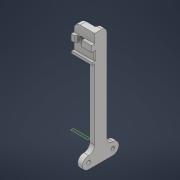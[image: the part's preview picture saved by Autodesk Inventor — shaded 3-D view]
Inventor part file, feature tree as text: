
AUTODESK INVENTOR PART (.ipt)
format: ipt  version: 2021 (Build 250183000, 183)  size: 370,688 bytes
history: native  units: mm
features: sketch x11, extrude x9, move_body x8, fillet x7, projected_geometry x7, direct_edit x5, hole x2, draft x2, chamfer x1, plane x1, split x1, mirror x1
ambient origin geometry x8: Origin, YZ Plane, XZ Plane, XY Plane, X Axis, Y Axis, Z Axis, Center Point
bodies: Solid1 (feature_tree)
feature tree (55):
  extrude  "Extrusion1"  Depth=10.0mm
  hole  "Hole1"  [1 undecoded]
  draft  "FaceDraft1"
  extrude  "Extrusion2"  Depth=10.0mm TaperAngle=0.0deg
  fillet  "Fillet2"  Radius=0.5mm
  extrude  "Extrusion3"  Depth=20.0mm
  extrude  "Extrusion4"  Depth=5.0mm
  extrude  "Extrusion5"  Depth=5.1mm
  extrude  "Extrusion6"  Depth=2.0mm TaperAngle=0.0deg
  fillet  "Fillet4"  Radius=1.0mm
  direct_edit  "Direct Edit1"
  chamfer  "Chamfer1"  Distance=1.0mm
  direct_edit  "Direct Edit2"
  plane  "Work Plane1"
  split  "Split1"
  extrude  "Extrusion7"  Depth=0.5mm TaperAngle=0.0deg
  hole  "Hole2"  [1 undecoded]
  direct_edit  "Direct Edit3"
  draft  "FaceDraft2"
  fillet  "Fillet5"  Radius=55.0mm
  direct_edit  "Direct Edit5"
  fillet  "Fillet7"  Radius=36.0mm
  fillet  "Fillet8"  Radius=30.0mm
  extrude  "Extrusion8"  Depth=20.0mm
  direct_edit  "Direct Edit6"
  extrude  "Extrusion9"  Depth=5.0mm
  fillet  "Fillet9"  Radius=5.0mm
  fillet  "Fillet10"  Radius=5.0mm
  mirror  "Mirror1"
  sketch  "Sketch1"  dims[d3=5.0mm d4=0.0mm d5=10.0mm]
  sketch  "Sketch2"  dims[d6=5.1mm d7=6.0mm d8=4.0mm d9=2.0mm d10=90.0deg d11=8.0mm d12=20.594885mm d14=15.0deg]
  sketch  "Sketch3"  dims[d15=0.6mm d16=10.0mm d17=0.0mm d18=0.5mm]
  sketch  "Sketch4"  dims[d19=10.0mm d21=20.0mm]
  sketch  "Sketch5"  dims[d22=2.0mm d23=5.0mm]
  projected_geometry  "Projected Loop1"
  sketch  "Sketch6"  dims[d24=2.0mm d25=0.0mm d26=5.1mm]
  projected_geometry  "Projected Loop2"
  projected_geometry  "Projected Loop3"
  sketch  "Sketch7"  dims[d27=5.1mm d28=2.0mm d29=0.0mm d32=1.0mm d33=0.0mm d34=1.0mm d35=0.0mm]
  projected_geometry  "Projected Loop4"
  projected_geometry  "Projected Loop5"
  sketch  "Sketch8"  dims[d36=1.0mm d37=0.0mm d38=0.0mm d39=0.5mm]
  sketch  "Sketch9"  dims[d40=1.5mm d41=2.0mm d42=45.0deg d43=0.0mm d44=0.0mm d45=0.5mm]
  sketch  "Sketch10"  dims[d46=0.0mm d47=0.0mm d48=0.5mm d49=55.0mm d50=36.0mm d51=30.0mm]
  projected_geometry  "Projected Loop6"
  sketch  "Sketch11"  dims[d52=3.0mm d53=0.0mm d54=20.0mm d55=5.0mm d56=5.0mm d57=5.0mm d58=5.0mm d59=3.0mm d60=6.0mm d61=4.0mm d62=2.0mm d63=90.0deg d64=8.0mm d65=20.594885mm d66=0.0mm d67=0.0mm d68=10.0mm d69=0.0mm d70=0.0mm d71=-5.0mm d72=4.363323mm d73=5.0mm d77=10.0mm d78=0.0mm d79=0.0mm d80=1.0mm d81=8.0mm d82=5.0mm d83=0.0mm d84=0.0mm d85=0.0mm d86=0.0mm d87=4.0mm d88=0.0mm d89=0.0mm d90=4.0mm d91=1.0mm d92=10.0mm d93=4.0mm d94=0.0mm d95=5.0mm d96=5.0mm d97=1.0mm]
  projected_geometry  "Projected Loop7"
  move_body  "Move1"
  move_body  "Move2"
  move_body  "Move3"
  move_body  "Move4"
  move_body  "Move5"
  move_body  "Move6"
  move_body  "Move7"
  move_body  "Move8"
note: 2 required parameter values undecoded (feature->parameter linkage not recoverable at this tier; creation-order binding heuristic only, values carry confidence <= 0.55)
